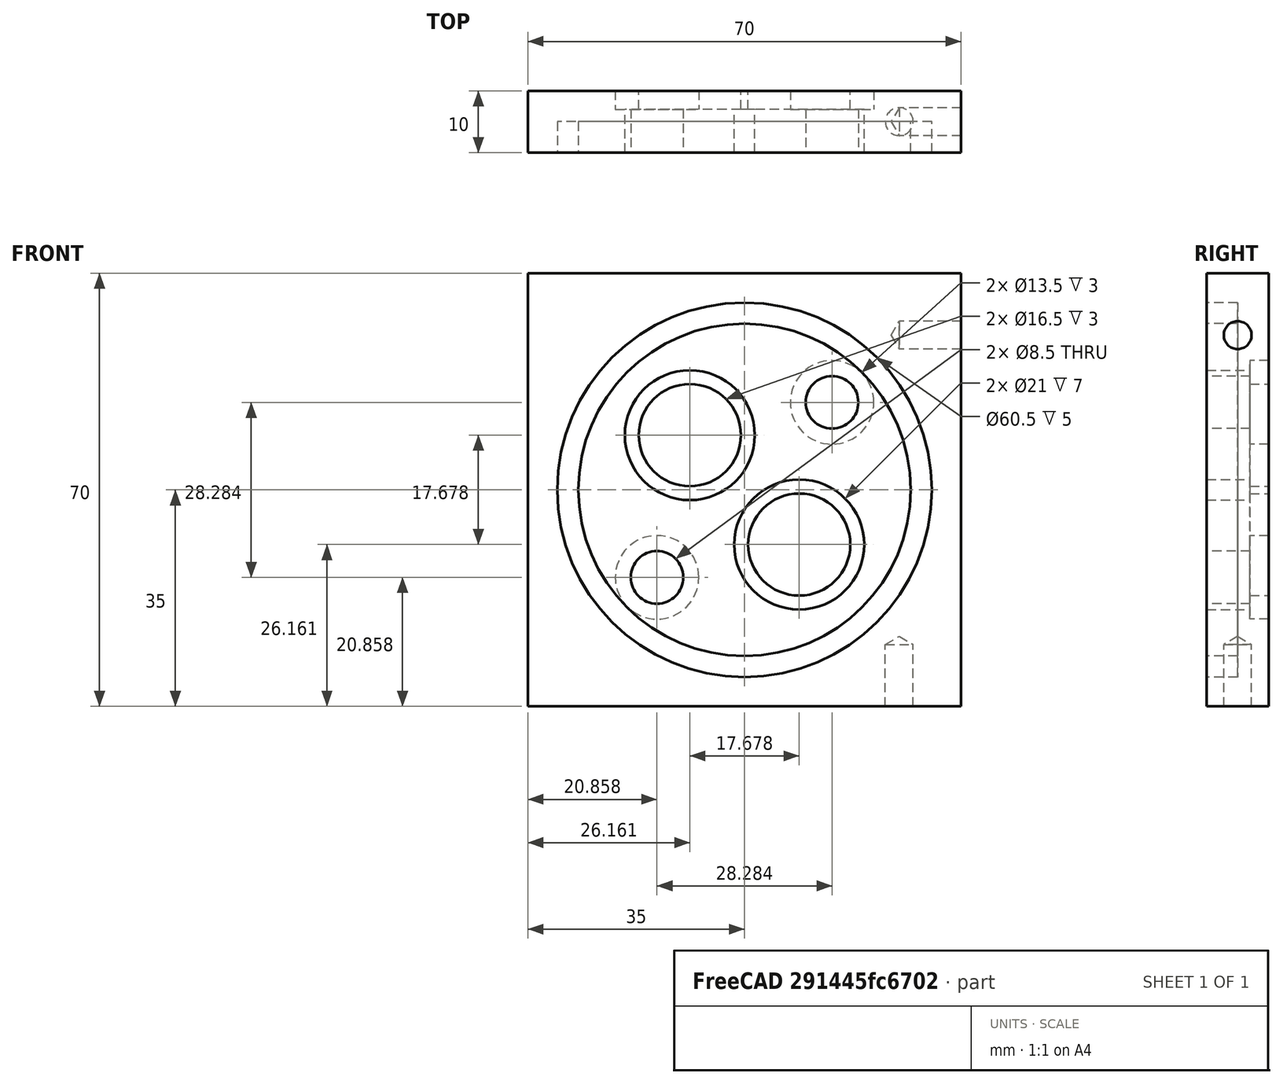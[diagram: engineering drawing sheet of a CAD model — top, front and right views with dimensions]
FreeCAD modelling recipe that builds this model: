
FCSTD DOCUMENT  (FreeCAD 0.21R33771 (Git))
Label: Deckelplatte M12
Comment: Silionring von Moka Pott 3 Cups Di 51mm, Da:65mm
License: All rights reserved
LicenseURL: http://en.wikipedia.org/wiki/All_rights_reserved
objects: TechDraw::DrawViewDimension×12, Sketcher::SketchObject×7, PartDesign::Hole×4, TechDraw::DrawProjGroupItem×4, TechDraw::DrawViewSection×2, PartDesign::Pad×1, PartDesign::Pocket×1, PartDesign::Body×1, TechDraw::DrawSVGTemplate×1, TechDraw::DrawProjGroup×1, TechDraw::DrawViewAnnotation×1, TechDraw::DrawViewPart×1, TechDraw::DrawPage×1
note: 20 computed .brp shape members not serialized (recipe doc carries the construction recipe); baked Part::Feature solids carry a one-line shape summary decoded from their .brp

FEATURE [Sketcher::SketchObject] Sketch
  FullyConstrained = true
  MapMode = 5
  Placement = pos=(0,0,0) rot=(1,0,0;1.5708rad)
  Support = -> [XZ_Plane]
  sketch-geometry (4):
    g0: LineSegment StartX=-35 StartY=35 StartZ=0 EndX=35 EndY=35 EndZ=0
    g1: LineSegment StartX=35 StartY=35 StartZ=0 EndX=35 EndY=-35 EndZ=0
    g2: LineSegment StartX=35 StartY=-35 StartZ=0 EndX=-35 EndY=-35 EndZ=0
    g3: LineSegment StartX=-35 StartY=-35 StartZ=0 EndX=-35 EndY=35 EndZ=0
  constraints (10):
    c: Coincident(g0,g1)
    c: Coincident(g1,g2)
    c: Coincident(g2,g3)
    c: Coincident(g3,g0)
    c: Horizontal(g2)
    c: Vertical(g3)
    c: Symmetric(g0,g0,g-2)
    c: Symmetric(g0,g1,g-1)
    c: DistanceX(g0,g0) = 70
    c: Equal(g1,g0)
FEATURE [PartDesign::Pad] Pad
  Direction = (0,-1,2e-16)
  Length = 10
  Length2 = 10
  Placement = pos=(0,0,0) rot=(1,0,0;1.5708rad)
  Profile = -> Sketch
  ReferenceAxis = -> Sketch [N_Axis]
  Type = 0
FEATURE [Sketcher::SketchObject] Sketch001
  FullyConstrained = true
  MapMode = 5
  Placement = pos=(0,-10,4.4e-15) rot=(1,0,0;1.5708rad)
  Support = -> [Pad]
  sketch-geometry (2):
    g0: Circle CenterX=0 CenterY=0 CenterZ=0 NormalX=0 NormalY=0 NormalZ=1 AngleXU=0 Radius=26.85
    g1: Circle CenterX=0 CenterY=0 CenterZ=0 NormalX=0 NormalY=0 NormalZ=1 AngleXU=0 Radius=30.25
  constraints (4):
    c: Coincident(g0,g-1)
    c: Coincident(g1,g0)
    c: Diameter(g1) = 60.5
    c: Diameter(g0) = 53.7
FEATURE [PartDesign::Pocket] Pocket
  BaseFeature = -> Pad
  Direction = (0,1,-4e-16)
  Length = 5
  Length2 = 5
  Placement = pos=(0,0,0) rot=(1,0,0;1.5708rad)
  Profile = -> Sketch001
  ReferenceAxis = -> Sketch001 [N_Axis]
  Type = 0
FEATURE [Sketcher::SketchObject] Sketch002
  FullyConstrained = true
  MapMode = 5
  Placement = pos=(0,-10,5.5e-15) rot=(1,0,0;1.5708rad)
  Support = -> [Pocket]
FEATURE [Sketcher::SketchObject] Sketch003
  ExternalGeometry = -> [Pocket]
  FullyConstrained = true
  MapMode = 5
  Placement = pos=(35,0,0) rot=(0.707107,0,0.707107;3.14159rad)
  Support = -> [Pocket]
  sketch-geometry (1):
    g0: Circle CenterX=25 CenterY=5 CenterZ=0 NormalX=0 NormalY=0 NormalZ=1 AngleXU=0 Radius=2
  constraints (3):
    c: Diameter(g0) = 4
    c: DistanceY(g-1,g0) = 5
    c: DistanceX(g0,g-3) = 10
FEATURE [PartDesign::Hole] Hole
  BaseFeature = -> Pocket
  CustomThreadClearance = 0
  Depth = 10
  DepthType = 0
  Diameter = 4.5
  DrillForDepth = false
  DrillPoint = 1
  DrillPointAngle = 118
  HoleCutCountersinkAngle = 90
  HoleCutCustomValues = false
  HoleCutDepth = 0
  HoleCutDiameter = 6.1
  HoleCutType = 0
  ModelThread = false
  Placement = pos=(0,0,0) rot=(1,0,0;1.5708rad)
  Profile = -> Sketch003
  Tapered = false
  TaperedAngle = 90
  ThreadClass = 0
  ThreadDepth = 10
  ThreadDepthType = 0
  ThreadDirection = 0
  ThreadFit = 0
  ThreadSize = 11
  ThreadType = 1
  Threaded = false
  UseCustomThreadClearance = false
FEATURE [Sketcher::SketchObject] Sketch004
  ExternalGeometry = -> [Hole]
  FullyConstrained = true
  MapMode = 5
  Placement = pos=(0,-3.09e-14,-35) rot=(1,0,0;3.14159rad)
  Support = -> [Hole]
  sketch-geometry (1):
    g0: Circle CenterX=25 CenterY=5 CenterZ=0 NormalX=0 NormalY=0 NormalZ=1 AngleXU=0 Radius=2
  constraints (3):
    c: DistanceX(g0,g-4) = 10
    c: DistanceY(g-5,g0) = 5
    c: Diameter(g0) = 4
FEATURE [PartDesign::Hole] Hole001
  BaseFeature = -> Hole
  CustomThreadClearance = 0
  Depth = 10
  DepthType = 0
  Diameter = 4.5
  DrillForDepth = false
  DrillPoint = 1
  DrillPointAngle = 118
  HoleCutCountersinkAngle = 90
  HoleCutCustomValues = false
  HoleCutDepth = 0
  HoleCutDiameter = 6.1
  HoleCutType = 0
  ModelThread = false
  Placement = pos=(0,0,0) rot=(1,0,0;1.5708rad)
  Profile = -> Sketch004
  Tapered = false
  TaperedAngle = 90
  ThreadClass = 0
  ThreadDepth = 10
  ThreadDepthType = 0
  ThreadDirection = 0
  ThreadFit = 0
  ThreadSize = 11
  ThreadType = 1
  Threaded = false
  UseCustomThreadClearance = false
FEATURE [Sketcher::SketchObject] Sketch006
  FullyConstrained = false
  MapMode = 5
  Placement = pos=(0,-10,7e-15) rot=(1,0,0;1.5708rad)
  sketch-geometry (3):
    g0: LineSegment StartX=-35 StartY=35 StartZ=0 EndX=35 EndY=-35 EndZ=0
    g1: Circle CenterX=-8.83883 CenterY=8.83883 CenterZ=0 NormalX=0 NormalY=0 NormalZ=1 AngleXU=0 Radius=11
    g2: Circle CenterX=8.83883 CenterY=-8.83883 CenterZ=0 NormalX=0 NormalY=0 NormalZ=1 AngleXU=0 Radius=11
  constraints (5):
    c: PointOnObject(g1,g0)
    c: Symmetric(g1,g2,g-1)
    c: Distance(g1,g2) = 25
    c: Diameter(g2) = 22
    c: Equal(g2,g1)
FEATURE [PartDesign::Hole] Hole003
  BaseFeature = -> Hole001
  CustomThreadClearance = 0
  Depth = 200.987
  DepthType = 1
  Diameter = 16.5
  DrillForDepth = false
  DrillPoint = 1
  DrillPointAngle = 118
  HoleCutCountersinkAngle = 90
  HoleCutCustomValues = false
  HoleCutDepth = 7
  HoleCutDiameter = 21
  HoleCutType = 1
  ModelThread = false
  Placement = pos=(0,0,0) rot=(1,0,0;1.5708rad)
  Profile = -> Sketch006
  Tapered = false
  TaperedAngle = 90
  ThreadClass = 0
  ThreadDepth = 200.987
  ThreadDepthType = 0
  ThreadDirection = 0
  ThreadFit = 0
  ThreadSize = 0
  ThreadType = 0
  Threaded = false
  UseCustomThreadClearance = false
FEATURE [Sketcher::SketchObject] Sketch007
  ExternalGeometry = -> [Hole003]
  FullyConstrained = true
  MapMode = 5
  Placement = pos=(0,0,0) rot=(-1,0,0;1.5708rad)
  Support = -> [Hole003]
  sketch-geometry (3):
    g0: LineSegment StartX=-35 StartY=35 StartZ=0 EndX=35 EndY=-35 EndZ=0
    g1: Circle CenterX=-14.1421 CenterY=14.1421 CenterZ=0 NormalX=0 NormalY=0 NormalZ=1 AngleXU=0 Radius=2.75
    g2: Circle CenterX=14.1421 CenterY=-14.1421 CenterZ=0 NormalX=0 NormalY=0 NormalZ=1 AngleXU=0 Radius=2.75
  constraints (7):
    c: Coincident(g0,g-3)
    c: Coincident(g0,g-4)
    c: PointOnObject(g1,g0)
    c: Symmetric(g1,g2,g-1)
    c: Distance(g1,g2) = 40
    c: Diameter(g2) = 5.5
    c: Equal(g2,g1)
FEATURE [PartDesign::Hole] Hole004
  BaseFeature = -> Hole003
  CustomThreadClearance = 0
  Depth = 200.987
  DepthType = 1
  Diameter = 8.5
  DrillForDepth = false
  DrillPoint = 1
  DrillPointAngle = 118
  HoleCutCountersinkAngle = 90
  HoleCutCustomValues = false
  HoleCutDepth = 3
  HoleCutDiameter = 13.5
  HoleCutType = 1
  ModelThread = false
  Placement = pos=(0,0,0) rot=(1,0,0;1.5708rad)
  Profile = -> Sketch007
  Tapered = false
  TaperedAngle = 90
  ThreadClass = 0
  ThreadDepth = 200.987
  ThreadDepthType = 0
  ThreadDirection = 0
  ThreadFit = 0
  ThreadSize = 0
  ThreadType = 0
  Threaded = false
  UseCustomThreadClearance = false
FEATURE [PartDesign::Body] Body
  Group = -> [Sketch,Pad,Sketch001,Pocket,Sketch002,Sketch003,Hole,Sketch004,Hole001,Sketch006,Hole003,Sketch007,Hole004]
  Origin = -> Origin
  Tip = -> Hole004
FEATURE [TechDraw::DrawSVGTemplate] Template
  EditableTexts = Approved1=Approved 1; Approved2=Approved 2; CheckedBy=Checked By; Code=Code; DrawingNumber=Drawing Number; DrawingTitle1=CANSpy; DrawingTitle2=M12 Plate; DrawingTitle3=-; DrawnBy=Drawn By; Revision=Rev; Scale=Scale; Sheet=Sheet n of m; Weight=Weight
  Height = 279.4
  Orientation = 1
  Width = 431.8
FEATURE [TechDraw::DrawProjGroupItem] ProjItem  label="Front"
  CoarseView = false
  Direction = (0,-1,0)
  Focus = 100
  HardHidden = false
  IsoCount = 0
  IsoHidden = false
  IsoVisible = false
  LockPosition = true
  Perspective = false
  Rotation = 0
  RotationVector = (1,0,0)
  ScaleType = 2
  ScrubCount = 0
  SeamHidden = false
  SeamVisible = true
  SmoothHidden = false
  SmoothVisible = true
  Source = -> [Body]
  Type = 0
  X = 0
  XDirection = (1,0,0)
  Y = 0
FEATURE [TechDraw::DrawProjGroupItem] ProjItem001  label="Bottom"
  CoarseView = false
  Direction = (0,0,-1)
  Focus = 100
  HardHidden = false
  IsoCount = 0
  IsoHidden = false
  IsoVisible = false
  LockPosition = false
  Perspective = false
  Rotation = 0
  RotationVector = (1,0,0)
  ScaleType = 2
  ScrubCount = 0
  SeamHidden = false
  SeamVisible = true
  SmoothHidden = false
  SmoothVisible = true
  Source = -> [Body]
  Type = 5
  X = 0
  XDirection = (1,0,0)
  Y = 55
FEATURE [TechDraw::DrawProjGroupItem] ProjItem002  label="Right"
  CoarseView = false
  Direction = (1,-1e-16,0)
  Focus = 100
  HardHidden = false
  IsoCount = 0
  IsoHidden = false
  IsoVisible = false
  LockPosition = false
  Perspective = false
  Rotation = 0
  RotationVector = (1,0,0)
  ScaleType = 2
  ScrubCount = 0
  SeamHidden = false
  SeamVisible = true
  SmoothHidden = false
  SmoothVisible = true
  Source = -> [Body]
  Type = 2
  X = -55
  XDirection = (1e-16,1,0)
  Y = 0
FEATURE [TechDraw::DrawProjGroupItem] ProjItem003  label="Rear"
  CoarseView = false
  Direction = (0,1,0)
  Focus = 100
  HardHidden = false
  IsoCount = 0
  IsoHidden = false
  IsoVisible = false
  LockPosition = false
  Perspective = false
  Rotation = 0
  RotationVector = (1,0,0)
  ScaleType = 2
  ScrubCount = 0
  SeamHidden = false
  SeamVisible = true
  SmoothHidden = false
  SmoothVisible = true
  Source = -> [Body]
  Type = 3
  X = 108.798
  XDirection = (-1,0,0)
  Y = 0
FEATURE [TechDraw::DrawProjGroup] ProjGroup
  Anchor = -> ProjItem
  AutoDistribute = true
  LockPosition = false
  ProjectionType = 0
  Rotation = 0
  ScaleType = 0
  Source = -> [Body]
  Views = -> [ProjItem,ProjItem001,ProjItem002,ProjItem003]
  X = 215.469
  Y = 139.818
  spacingX = 15
  spacingY = 15
FEATURE [TechDraw::DrawViewDimension] Dimension
  AngleOverride = false
  Arbitrary = false
  ArbitraryTolerances = false
  EqualTolerance = true
  ExtensionAngle = 0
  FormatSpec = %.2w
  FormatSpecOverTolerance = %+.2w
  FormatSpecUnderTolerance = %+.2w
  Inverted = false
  LineAngle = 0
  LockPosition = false
  MeasureType = 1
  OverTolerance = 0
  References2D = -> [ProjItem003]
  Rotation = 0
  ScaleType = 0
  TheoreticalExact = false
  Type = 2
  UnderTolerance = 0
  X = 51.7799
  Y = 1.72203
FEATURE [TechDraw::DrawViewDimension] Dimension001
  AngleOverride = false
  Arbitrary = false
  ArbitraryTolerances = false
  EqualTolerance = true
  ExtensionAngle = 0
  FormatSpec = R%.2w
  FormatSpecOverTolerance = %+.2w
  FormatSpecUnderTolerance = %+.2w
  Inverted = false
  LineAngle = 0
  LockPosition = false
  MeasureType = 1
  OverTolerance = 0
  References2D = -> [ProjItem003]
  Rotation = 0
  ScaleType = 0
  TheoreticalExact = false
  Type = 4
  UnderTolerance = 0
  X = 22.9139
  Y = 7.10707
FEATURE [TechDraw::DrawViewDimension] Dimension002
  AngleOverride = false
  Arbitrary = false
  ArbitraryTolerances = false
  EqualTolerance = true
  ExtensionAngle = 0
  FormatSpec = R%.2w
  FormatSpecOverTolerance = %+.2w
  FormatSpecUnderTolerance = %+.2w
  Inverted = false
  LineAngle = 0
  LockPosition = false
  MeasureType = 1
  OverTolerance = 0
  References2D = -> [ProjItem003]
  Rotation = 0
  ScaleType = 0
  TheoreticalExact = false
  Type = 4
  UnderTolerance = 0
  X = -2.07842
  Y = -18.1026
FEATURE [TechDraw::DrawViewDimension] Dimension003
  AngleOverride = false
  Arbitrary = false
  ArbitraryTolerances = false
  EqualTolerance = true
  ExtensionAngle = 0
  FormatSpec = R%.2w
  FormatSpecOverTolerance = %+.2w
  FormatSpecUnderTolerance = %+.2w
  Inverted = false
  LineAngle = 0
  LockPosition = false
  MeasureType = 1
  OverTolerance = 0
  References2D = -> [ProjItem]
  Rotation = 0
  ScaleType = 0
  TheoreticalExact = false
  Type = 4
  UnderTolerance = 0
  X = -1.83441
  Y = -19.1302
FEATURE [TechDraw::DrawViewDimension] Dimension004
  AngleOverride = false
  Arbitrary = false
  ArbitraryTolerances = false
  EqualTolerance = true
  ExtensionAngle = 0
  FormatSpec = R%.2w
  FormatSpecOverTolerance = %+.2w
  FormatSpecUnderTolerance = %+.2w
  Inverted = false
  LineAngle = 0
  LockPosition = false
  MeasureType = 1
  OverTolerance = 0
  References2D = -> [ProjItem]
  Rotation = 0
  ScaleType = 0
  TheoreticalExact = false
  Type = 4
  UnderTolerance = 0
  X = -7.59968
  Y = -14.4132
FEATURE [TechDraw::DrawViewDimension] Dimension005
  AngleOverride = false
  Arbitrary = false
  ArbitraryTolerances = false
  EqualTolerance = true
  ExtensionAngle = 0
  FormatSpec = %.2w
  FormatSpecOverTolerance = %+.2w
  FormatSpecUnderTolerance = %+.2w
  Inverted = false
  LineAngle = 0
  LockPosition = false
  MeasureType = 1
  OverTolerance = 0
  References2D = -> [ProjItem]
  Rotation = 0
  ScaleType = 0
  TheoreticalExact = false
  Type = 2
  UnderTolerance = 0
  X = 39.5332
  Y = -18.1009
FEATURE [TechDraw::DrawViewDimension] Dimension006
  AngleOverride = false
  Arbitrary = false
  ArbitraryTolerances = false
  EqualTolerance = true
  ExtensionAngle = 0
  FormatSpec = %.2w
  FormatSpecOverTolerance = %+.2w
  FormatSpecUnderTolerance = %+.2w
  Inverted = false
  LineAngle = 0
  LockPosition = false
  MeasureType = 1
  OverTolerance = 0
  References2D = -> [ProjItem]
  Rotation = 0
  ScaleType = 0
  TheoreticalExact = false
  Type = 2
  UnderTolerance = 0
  X = -49.3707
  Y = -24.1469
FEATURE [TechDraw::DrawViewDimension] Dimension007
  AngleOverride = false
  Arbitrary = false
  ArbitraryTolerances = false
  EqualTolerance = true
  ExtensionAngle = 0
  FormatSpec = R%.2w
  FormatSpecOverTolerance = %+.2w
  FormatSpecUnderTolerance = %+.2w
  Inverted = false
  LineAngle = 0
  LockPosition = false
  MeasureType = 1
  OverTolerance = 0
  References2D = -> [ProjItem]
  Rotation = 0
  ScaleType = 0
  TheoreticalExact = false
  Type = 4
  UnderTolerance = 0
  X = 40.8811
  Y = 26.4679
FEATURE [TechDraw::DrawViewDimension] Dimension008
  AngleOverride = false
  Arbitrary = false
  ArbitraryTolerances = false
  EqualTolerance = true
  ExtensionAngle = 0
  FormatSpec = R%.2w
  FormatSpecOverTolerance = %+.2w
  FormatSpecUnderTolerance = %+.2w
  Inverted = false
  LineAngle = 0
  LockPosition = false
  MeasureType = 1
  OverTolerance = 0
  References2D = -> [ProjItem]
  Rotation = 0
  ScaleType = 0
  TheoreticalExact = false
  Type = 4
  UnderTolerance = 0
  X = 11.5306
  Y = 46.3843
FEATURE [TechDraw::DrawViewAnnotation] Annotation
  Font = osifont
  LineSpace = 80
  LockPosition = false
  MaxWidth = -1
  Rotation = 0
  ScaleType = 0
  Text = M4 | Blind hole
  TextSize = 5
  TextStyle = 0
  X = 148.602
  Y = 157.806
FEATURE [TechDraw::DrawViewDimension] Dimension009
  AngleOverride = false
  Arbitrary = false
  ArbitraryTolerances = false
  EqualTolerance = true
  ExtensionAngle = 0
  FormatSpec = %.2w
  FormatSpecOverTolerance = %+.2w
  FormatSpecUnderTolerance = %+.2w
  Inverted = false
  LineAngle = 0
  LockPosition = false
  MeasureType = 1
  OverTolerance = 0
  References2D = -> [ProjItem002]
  Rotation = 0
  ScaleType = 0
  TheoreticalExact = false
  Type = 2
  UnderTolerance = 0
  X = -18.8315
  Y = 30.4413
FEATURE [TechDraw::DrawViewSection] SectionView  label="Section  - "
  BaseView = -> ProjItem001
  CoarseView = false
  CutSurfaceDisplay = 2
  Direction = (0,1,0)
  FileGeomPattern = <path>
  FileHatchPattern = <path>
  Focus = 100
  FuseBeforeCut = false
  HardHidden = false
  HatchOffset = (0,0,0)
  HatchRotation = 0
  HatchScale = 1
  IsoCount = 0
  IsoHidden = false
  IsoVisible = false
  LockPosition = false
  NameGeomPattern = Diamond
  Perspective = false
  Rotation = 0
  ScaleType = 2
  ScrubCount = 0
  SeamHidden = false
  SeamVisible = true
  SectionDirection = 2
  SectionNormal = (0,1,0)
  SectionOrigin = (0.008,-5,-0.008)
  SmoothHidden = false
  SmoothVisible = true
  Source = -> [Body]
  TrimAfterCut = false
  X = 67.1432
  XDirection = (1,0,0)
  Y = 138.986
FEATURE [TechDraw::DrawViewSection] SectionView001  label="Section  - 001"
  BaseView = -> ProjItem
  CoarseView = false
  CutSurfaceDisplay = 2
  Direction = (0,0,-1)
  FileGeomPattern = <path>
  FileHatchPattern = <path>
  Focus = 100
  FuseBeforeCut = false
  HardHidden = false
  HatchOffset = (0,0,0)
  HatchRotation = 0
  HatchScale = 1
  IsoCount = 0
  IsoHidden = false
  IsoVisible = false
  LockPosition = false
  NameGeomPattern = Diamond
  Perspective = false
  Rotation = 0
  ScaleType = 2
  ScrubCount = 0
  SeamHidden = false
  SeamVisible = true
  SectionDirection = 2
  SectionNormal = (0,0,-1)
  SectionOrigin = (0,-5,-12)
  SmoothHidden = false
  SmoothVisible = true
  Source = -> [Body]
  TrimAfterCut = false
  X = 212.18
  XDirection = (1,0,0)
  Y = 74.7992
FEATURE [TechDraw::DrawViewDimension] Dimension010
  AngleOverride = false
  Arbitrary = false
  ArbitraryTolerances = false
  EqualTolerance = true
  ExtensionAngle = 0
  FormatSpec = %.2w
  FormatSpecOverTolerance = %+.2w
  FormatSpecUnderTolerance = %+.2w
  Inverted = false
  LineAngle = 0
  LockPosition = false
  MeasureType = 1
  OverTolerance = 0
  References2D = -> [SectionView001]
  Rotation = 0
  ScaleType = 0
  TheoreticalExact = false
  Type = 2
  UnderTolerance = 0
  X = 44.2049
  Y = 6.75267
FEATURE [TechDraw::DrawViewDimension] Dimension011
  AngleOverride = false
  Arbitrary = false
  ArbitraryTolerances = false
  EqualTolerance = true
  ExtensionAngle = 0
  FormatSpec = %.2w
  FormatSpecOverTolerance = %+.2w
  FormatSpecUnderTolerance = %+.2w
  Inverted = false
  LineAngle = 0
  LockPosition = false
  MeasureType = 1
  OverTolerance = 0
  References2D = -> [ProjItem001]
  Rotation = 0
  ScaleType = 0
  TheoreticalExact = false
  Type = 2
  UnderTolerance = 0
  X = 37.9821
  Y = 17.8493
FEATURE [TechDraw::DrawViewPart] View
  CoarseView = false
  Direction = (0.413,-0.809,-0.419)
  Focus = 100
  HardHidden = false
  IsoCount = 0
  IsoHidden = false
  IsoVisible = false
  LockPosition = false
  Perspective = false
  Rotation = 0
  ScaleType = 0
  ScrubCount = 0
  SeamHidden = false
  SeamVisible = true
  SmoothHidden = false
  SmoothVisible = true
  Source = -> [Body]
  X = 96.9
  XDirection = (0.906,0.32,0.276)
  Y = 218.7
FEATURE [TechDraw::DrawPage] Page  label="2D-Zeichnung"
  KeepUpdated = true
  NextBalloonIndex = 1
  ProjectionType = 0
  Template = -> Template
  Views = -> [ProjGroup,Dimension,Dimension001,Dimension002,Dimension003,Dimension004,Dimension005,Dimension006,Dimension007,Dimension008,Annotation,Dimension009,SectionView,SectionView001,Dimension010,Dimension011,View]
note: 4 file-system paths scrubbed to <path> (originals preserved in the JSON sidecar)
